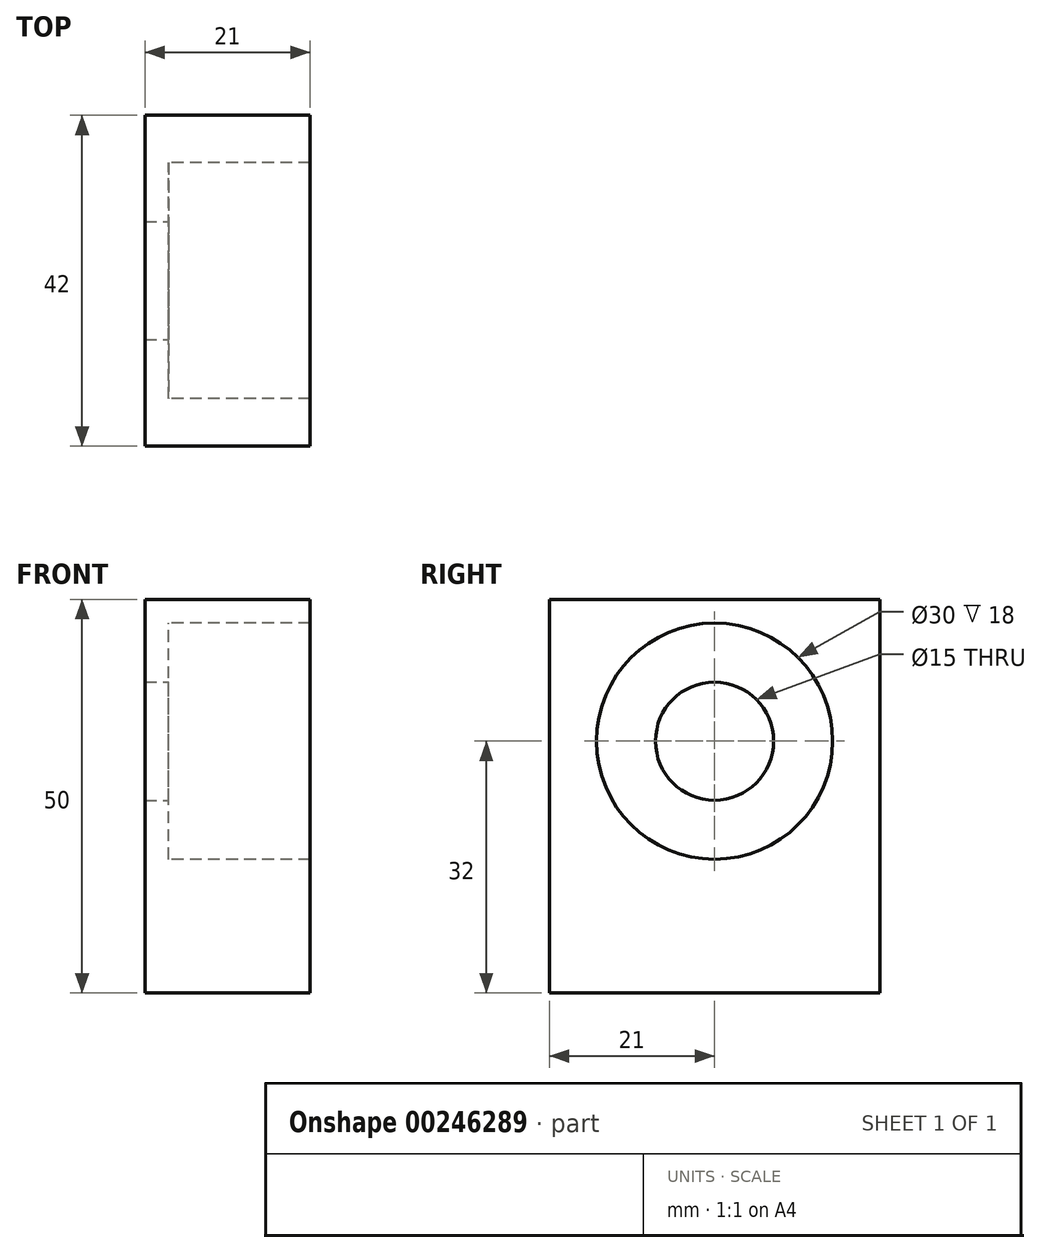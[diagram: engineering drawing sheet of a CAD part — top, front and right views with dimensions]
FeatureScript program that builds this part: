
annotation { "Feature Type Name" : "Feature", "Feature Type Description" : "" }
export const myFeature = defineFeature(function(context is Context, id is Id, definition is map)
    precondition{}
    {
        {
            var Q0;
            Q0=qCreatedBy(makeId("Right.planeOp"),FACE);
            var sketch = newSketch(context, id + "F0", { "sketchPlane" : qUnion([Q0])});
            skLineSegment(sketch, "E0.bottom", {"start": v(-21, 50) * mm, "end": v(21, 50) * mm});
            skLineSegment(sketch, "E0.top", {"start": v(-21, 0) * mm, "end": v(21, 0) * mm});
            skLineSegment(sketch, "E0.left", {"start": v(-21, 50) * mm, "end": v(-21, 0) * mm});
            skLineSegment(sketch, "E0.right", {"start": v(21, 50) * mm, "end": v(21, 0) * mm});
            skPoint(sketch, "E1", {"position": v(0, 50) * mm});
            skCircle(sketch, "E2", {"center": v(0, 32) * mm, "radius": 15 * mm});
            skCircle(sketch, "E3", {"center": v(0, 32) * mm, "radius": 7.5 * mm});
            skSolve(sketch);
        }
        {
            var Q0;
            Q0 = qSketchRegion(id + "F0", true);
            extrude(context, id + "F1", {"entities" : qUnion([Q0]), "depth" : 18 * mm});
        }
        {
            var Q0;
            Q0=makeQuery(id+"F0.imprint","IMPRINT",FACE,{"disambiguationData":[TD([[makeQuery(id+"F0.imprint","IMPRINT",EDGE,{"derivedFrom":sQuery(id+"F0.wireOp",EDGE,"E0.bottom")}),-1.0]])]});
            var Q1;
            Q1=makeQuery(id+"F0.imprint","IMPRINT",FACE,{"disambiguationData":[TD([[makeQuery(id+"F0.imprint","IMPRINT",EDGE,{"derivedFrom":sQuery(id+"F0.wireOp",EDGE,"E2")}),1.0]])]});
            extrude(context, id + "F2", {"entities" : qUnion([Q0, Q1]), "operationType" : NewBodyOperationType.ADD, "oppositeDirection" : true, "depth" : 3 * mm});
        }
    });
